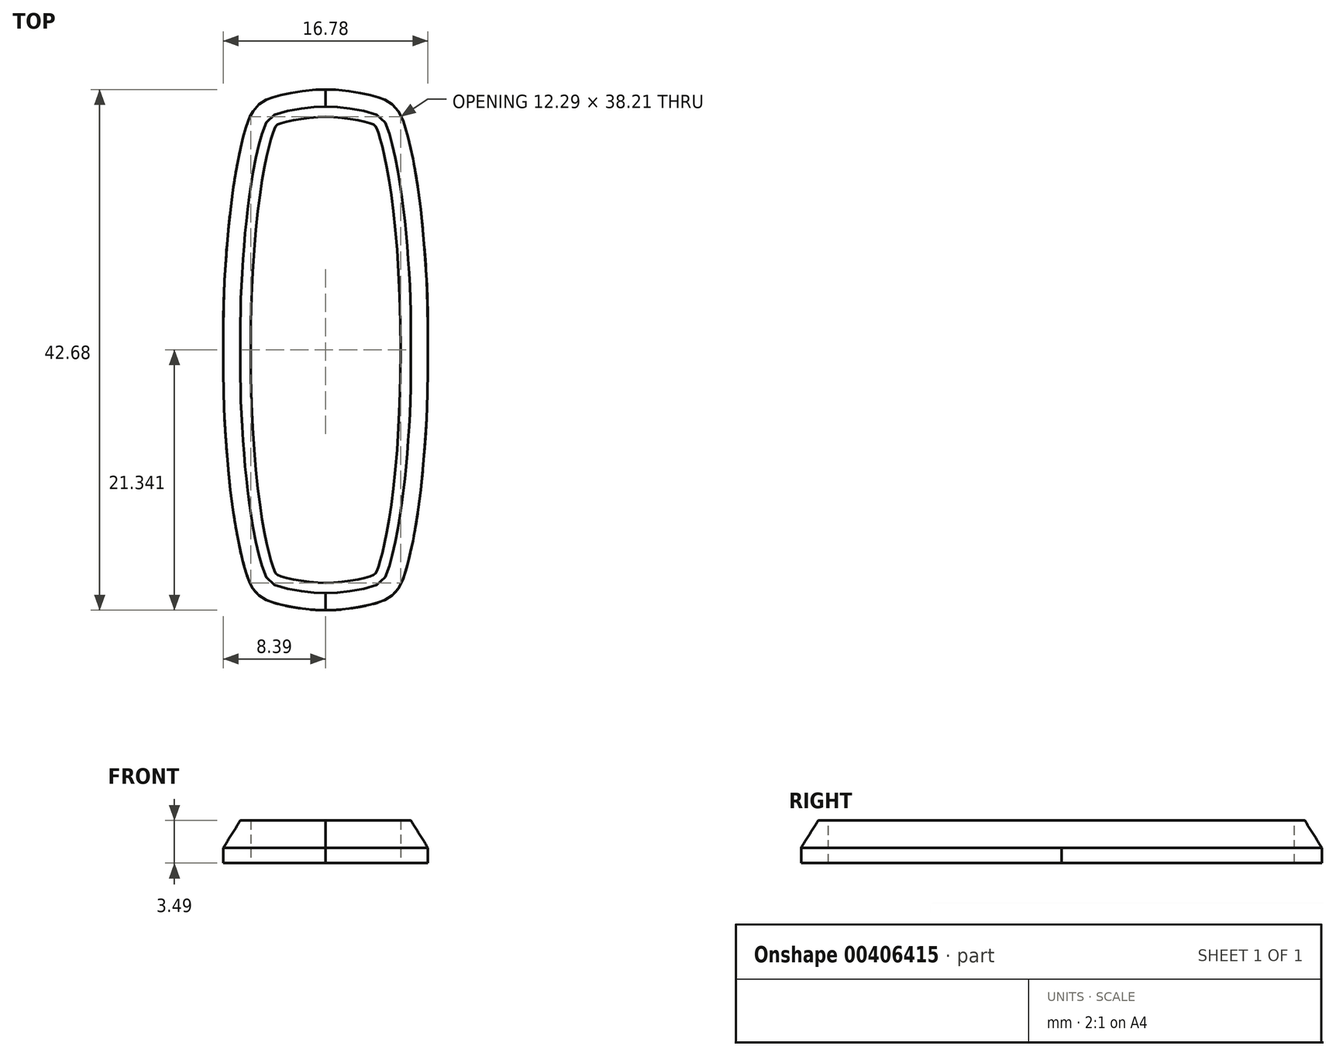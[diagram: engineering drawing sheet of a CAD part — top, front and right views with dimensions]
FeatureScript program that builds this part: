
annotation { "Feature Type Name" : "Feature", "Feature Type Description" : "" }
export const myFeature = defineFeature(function(context is Context, id is Id, definition is map)
    precondition{}
    {
        {
            var Q0;
            Q0=qCreatedBy(makeId("Top.planeOp"),FACE);
            var sketch = newSketch(context, id + "F0", { "sketchPlane" : qUnion([Q0])});
            skLineSegment(sketch, "E0", {"start": v(0, 0) * mm, "end": v(0, 33.02) * mm, "construction": true});
            skLineSegment(sketch, "E1", {"start": v(-5.59, 16.51) * mm, "end": v(-5.59, 16.51) * mm});
            skPoint(sketch, "E1.startSnap0", {"position": v(0, 16.51) * mm});
            skPoint(sketch, "E1.endSnap0", {"position": v(0, 16.51) * mm});
            skLineSegment(sketch, "E2", {"start": v(-3.75, 33.3) * mm, "end": v(0, 33.88) * mm, "construction": true});
            skLineSegment(sketch, "E3", {"start": v(0, 33.88) * mm, "end": v(0, 33.02) * mm, "construction": true});
            skFitSpline(sketch, "E4", {"points": [v(0, 33.88) * mm, v(-3.44, 33.36) * mm, v(-3.82, 32.96) * mm, v(-5.59, 16.51) * mm], "startDerivative": vector(-13.02, 0) * mm, "endDerivative": vector(0, -49.6) * mm});
            skFitSpline(sketch, "E5.MirrorCS", {"points": [v(0, 33.88) * mm, v(3.44, 33.36) * mm, v(3.82, 32.96) * mm, v(5.59, 16.51) * mm], "startDerivative": vector(13.02, 0) * mm, "endDerivative": vector(0, -49.6) * mm});
            skLineSegment(sketch, "E6", {"start": v(0, 16.51) * mm, "end": v(-16.2, 16.51) * mm, "construction": true});
            skFitSpline(sketch, "E7.MirrorCS", {"points": [v(0, -0.86) * mm, v(-3.44, -0.34) * mm, v(-3.82, 0.06) * mm, v(-5.59, 16.51) * mm], "startDerivative": vector(-13.02, 0) * mm, "endDerivative": vector(0, 49.6) * mm});
            skFitSpline(sketch, "E8.MirrorCS", {"points": [v(0, -0.86) * mm, v(3.44, -0.34) * mm, v(3.82, 0.06) * mm, v(5.59, 16.51) * mm], "startDerivative": vector(13.02, 0) * mm, "endDerivative": vector(0, 49.6) * mm});
            skFitSpline(sketch, "E9.0", {"points": [v(0, 35.9) * mm, v(-0.34, 35.9) * mm, v(-1.03, 35.87) * mm, v(-1.89, 35.77) * mm, v(-2.53, 35.67) * mm, v(-3, 35.58) * mm, v(-3.42, 35.49) * mm, v(-3.75, 35.4) * mm, v(-4.01, 35.31) * mm, v(-4.21, 35.24) * mm, v(-4.45, 35.13) * mm, v(-4.74, 34.97) * mm, v(-5.05, 34.73) * mm, v(-5.32, 34.43) * mm, v(-5.51, 34.14) * mm, v(-5.61, 33.94) * mm, v(-5.67, 33.82) * mm, v(-5.7, 33.74) * mm, v(-5.73, 33.66) * mm, v(-5.77, 33.56) * mm, v(-5.82, 33.43) * mm, v(-5.9, 33.2) * mm, v(-6, 32.9) * mm, v(-6.11, 32.46) * mm, v(-6.24, 31.98) * mm, v(-6.36, 31.43) * mm, v(-6.5, 30.81) * mm, v(-6.66, 29.9) * mm, v(-6.87, 28.61) * mm, v(-7.11, 26.78) * mm, v(-7.32, 24.66) * mm, v(-7.54, 21.46) * mm, v(-7.62, 18.61) * mm, v(-7.62, 16.51) * mm]});
            skFitSpline(sketch, "E9.1", {"points": [v(0, 35.9) * mm, v(0.34, 35.9) * mm, v(1.03, 35.87) * mm, v(1.89, 35.77) * mm, v(2.53, 35.67) * mm, v(3, 35.58) * mm, v(3.42, 35.49) * mm, v(3.75, 35.4) * mm, v(4.01, 35.31) * mm, v(4.21, 35.24) * mm, v(4.45, 35.13) * mm, v(4.74, 34.97) * mm, v(5.05, 34.73) * mm, v(5.32, 34.43) * mm, v(5.51, 34.14) * mm, v(5.61, 33.94) * mm, v(5.67, 33.82) * mm, v(5.7, 33.74) * mm, v(5.73, 33.66) * mm, v(5.77, 33.56) * mm, v(5.82, 33.43) * mm, v(5.9, 33.2) * mm, v(6, 32.9) * mm, v(6.11, 32.46) * mm, v(6.24, 31.98) * mm, v(6.36, 31.43) * mm, v(6.5, 30.81) * mm, v(6.66, 29.9) * mm, v(6.87, 28.61) * mm, v(7.11, 26.78) * mm, v(7.32, 24.66) * mm, v(7.54, 21.46) * mm, v(7.62, 18.61) * mm, v(7.62, 16.51) * mm]});
            skFitSpline(sketch, "E9.2", {"points": [v(0, -2.89) * mm, v(0.34, -2.89) * mm, v(1.03, -2.85) * mm, v(1.89, -2.75) * mm, v(2.53, -2.65) * mm, v(3, -2.56) * mm, v(3.42, -2.47) * mm, v(3.75, -2.38) * mm, v(4.01, -2.3) * mm, v(4.21, -2.22) * mm, v(4.45, -2.11) * mm, v(4.74, -1.95) * mm, v(5.05, -1.71) * mm, v(5.32, -1.4) * mm, v(5.51, -1.12) * mm, v(5.61, -0.92) * mm, v(5.67, -0.8) * mm, v(5.7, -0.72) * mm, v(5.73, -0.64) * mm, v(5.77, -0.54) * mm, v(5.82, -0.4) * mm, v(5.9, -0.18) * mm, v(6, 0.13) * mm, v(6.11, 0.56) * mm, v(6.24, 1.04) * mm, v(6.36, 1.6) * mm, v(6.5, 2.2) * mm, v(6.66, 3.11) * mm, v(6.87, 4.4) * mm, v(7.11, 6.24) * mm, v(7.32, 8.36) * mm, v(7.54, 11.56) * mm, v(7.62, 14.4) * mm, v(7.62, 16.51) * mm]});
            skFitSpline(sketch, "E9.3", {"points": [v(0, -2.89) * mm, v(-0.34, -2.89) * mm, v(-1.03, -2.85) * mm, v(-1.89, -2.75) * mm, v(-2.53, -2.65) * mm, v(-3, -2.56) * mm, v(-3.42, -2.47) * mm, v(-3.75, -2.38) * mm, v(-4.01, -2.3) * mm, v(-4.21, -2.22) * mm, v(-4.45, -2.11) * mm, v(-4.74, -1.95) * mm, v(-5.05, -1.71) * mm, v(-5.32, -1.4) * mm, v(-5.51, -1.12) * mm, v(-5.61, -0.92) * mm, v(-5.67, -0.8) * mm, v(-5.7, -0.72) * mm, v(-5.73, -0.64) * mm, v(-5.77, -0.54) * mm, v(-5.82, -0.4) * mm, v(-5.9, -0.18) * mm, v(-6, 0.13) * mm, v(-6.11, 0.56) * mm, v(-6.24, 1.04) * mm, v(-6.36, 1.6) * mm, v(-6.5, 2.2) * mm, v(-6.66, 3.11) * mm, v(-6.87, 4.4) * mm, v(-7.11, 6.24) * mm, v(-7.32, 8.36) * mm, v(-7.54, 11.56) * mm, v(-7.62, 14.4) * mm, v(-7.62, 16.51) * mm]});
            skSolve(sketch);
        }
        {
            var Q0;
            Q0=makeQuery(id+"F0.imprint","IMPRINT",FACE,{"disambiguationData":[TD([[makeQuery(id+"F0.imprint","IMPRINT",EDGE,{"derivedFrom":sQuery(id+"F0.wireOp",EDGE,"E4")}),-1.0]])]});
            extrude(context, id + "F1", {"entities" : qUnion([Q0]), "depth" : 3.17 * mm});
        }
        {
            var Q0;
            Q0=makeQuery(id+"F1.opExtrude","CAP_EDGE",EDGE,{"disambiguationData":[OSD([sQuery(id+"F0.wireOp",EDGE,"E9.3")])],"isStart":false});
            var Q1;
            Q1=makeQuery(id+"F1.opExtrude","CAP_EDGE",EDGE,{"disambiguationData":[OSD([sQuery(id+"F0.wireOp",EDGE,"E9.2")])],"isStart":false});
            var Q2;
            Q2=makeQuery(id+"F1.opExtrude","CAP_EDGE",EDGE,{"disambiguationData":[OSD([sQuery(id+"F0.wireOp",EDGE,"E9.1")])],"isStart":false});
            var Q3;
            Q3=makeQuery(id+"F1.opExtrude","CAP_EDGE",EDGE,{"disambiguationData":[OSD([sQuery(id+"F0.wireOp",EDGE,"E9.0")])],"isStart":false});
            chamfer(context, id + "F2", {"entities" : qUnion([Q0, Q1, Q2, Q3]), "chamferType" : ChamferType.TWO_OFFSETS, "width1" : 2.03 * mm, "oppositeDirection" : false, "width2" : 1.27 * mm, "tangentPropagation" : true});
        }
        {
            var Q0;
            Q0=makeQuery(id+"F1.opExtrude","SWEPT_BODY",BODY,{"disambiguationData":[OSD([sQuery(id+"F0.wireOp",EDGE,"E4"),sQuery(id+"F0.wireOp",EDGE,"E5.MirrorCS"),sQuery(id+"F0.wireOp",EDGE,"E7.MirrorCS"),sQuery(id+"F0.wireOp",EDGE,"E8.MirrorCS"),sQuery(id+"F0.wireOp",EDGE,"E9.0"),sQuery(id+"F0.wireOp",EDGE,"E9.1"),sQuery(id+"F0.wireOp",EDGE,"E9.2"),sQuery(id+"F0.wireOp",EDGE,"E9.3")])]});
            var Q1;
            Q1=qCreatedBy(makeId("Origin.pointOp"),VERTEX);
            transform(context, id + "F3", {"entities" : qUnion([Q0]), "transformType" : TransformType.SCALE_UNIFORMLY, "scale" : 1.1, "scalePoint" : qUnion([Q1]), "makeCopy" : false});
        }
    });
